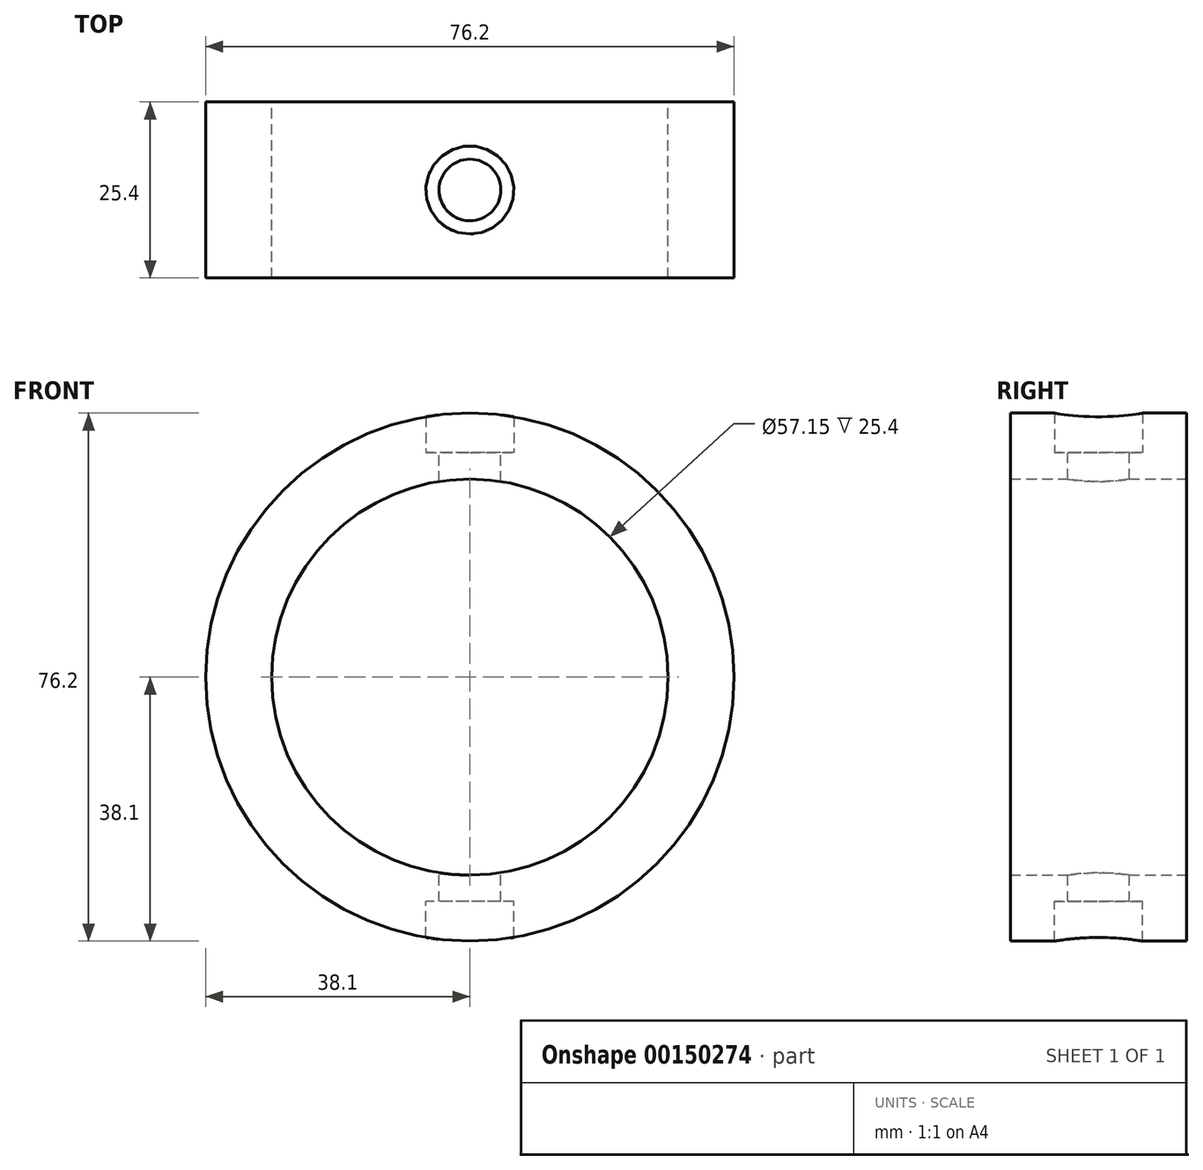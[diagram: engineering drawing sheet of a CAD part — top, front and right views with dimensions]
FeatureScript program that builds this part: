
annotation { "Feature Type Name" : "Feature", "Feature Type Description" : "" }
export const myFeature = defineFeature(function(context is Context, id is Id, definition is map)
    precondition{}
    {
        {
            var Q0;
            Q0=qCreatedBy(makeId("Front.planeOp"),FACE);
            var sketch = newSketch(context, id + "F0", { "sketchPlane" : qUnion([Q0])});
            skCircle(sketch, "E0", {"center": v(0, 0) * mm, "radius": 38.1 * mm});
            skCircle(sketch, "E1", {"center": v(0, 0) * mm, "radius": 28.58 * mm});
            skSolve(sketch);
        }
        {
            var Q0;
            Q0=makeQuery(id+"F0.imprint","IMPRINT",FACE,{"disambiguationData":[TD([[makeQuery(id+"F0.imprint","IMPRINT",EDGE,{"derivedFrom":sQuery(id+"F0.wireOp",EDGE,"E0")}),1.0]])]});
            extrude(context, id + "F1", {"entities" : qUnion([Q0]), "depth" : 25.4 * mm});
        }
        {
            var Q0;
            Q0=qCreatedBy(makeId("Top.planeOp"),FACE);
            var sketch = newSketch(context, id + "F2", { "sketchPlane" : qUnion([Q0])});
            skCircle(sketch, "E2", {"center": v(0, -12.7) * mm, "radius": 4.44 * mm});
            skLineSegment(sketch, "E3", {"start": v(38.1, 0) * mm, "end": v(38.1, -25.4) * mm});
            skLineSegment(sketch, "E4", {"start": v(-38.1, -25.4) * mm, "end": v(-38.1, 0) * mm});
            skSolve(sketch);
        }
        {
            var Q0;
            Q0=makeQuery(id+"F2.imprint","IMPRINT",FACE,{"disambiguationData":[TD([[makeQuery(id+"F2.imprint","IMPRINT",EDGE,{"derivedFrom":sQuery(id+"F2.wireOp",EDGE,"E2")}),1.0]])]});
            extrude(context, id + "F3", {"entities" : qUnion([Q0]), "operationType" : NewBodyOperationType.REMOVE, "endBound" : BoundingType.SYMMETRIC, "oppositeDirection" : true, "depth" : 76.2 * mm});
        }
        {
            var Q0;
            Q0=qCreatedBy(makeId("Top.planeOp"),FACE);
            cPlane(context, id + "F4", {"entities" : qUnion([Q0]), "cplaneType" : CPlaneType.OFFSET, "offset" : 32.38 * mm, "width" : 152.4 * mm, "height" : 152.4 * mm});
        }
        {
            var Q0;
            Q0=qCreatedBy(id+"F4.planeOp",FACE);
            var sketch = newSketch(context, id + "F5", { "sketchPlane" : qUnion([Q0])});
            skCircle(sketch, "E5", {"center": v(0, -12.7) * mm, "radius": 6.35 * mm});
            skLineSegment(sketch, "E6", {"start": v(38.1, 0) * mm, "end": v(38.1, -25.4) * mm});
            skLineSegment(sketch, "E7", {"start": v(-38.1, -25.4) * mm, "end": v(-38.1, 0) * mm});
            skCircle(sketch, "E8.0", {"center": v(0, -12.7) * mm, "radius": 4.44 * mm});
            skSolve(sketch);
        }
        {
            var Q0;
            Q0 = qSketchRegion(id + "F5", true);
            extrude(context, id + "F6", {"entities" : qUnion([Q0]), "operationType" : NewBodyOperationType.REMOVE, "depth" : 25.4 * mm});
        }
        {
            var Q0;
            Q0=qCreatedBy(makeId("Top.planeOp"),FACE);
            cPlane(context, id + "F7", {"entities" : qUnion([Q0]), "cplaneType" : CPlaneType.OFFSET, "offset" : 32.38 * mm, "oppositeDirection" : true, "width" : 152.4 * mm, "height" : 152.4 * mm});
        }
        {
            var Q0;
            Q0=qCreatedBy(id+"F7.planeOp",FACE);
            var sketch = newSketch(context, id + "F8", { "sketchPlane" : qUnion([Q0])});
            skCircle(sketch, "E9", {"center": v(0, -12.7) * mm, "radius": 6.35 * mm});
            skCircle(sketch, "E10.0", {"center": v(0, -12.7) * mm, "radius": 4.44 * mm});
            skSolve(sketch);
        }
        {
            var Q0;
            Q0 = qSketchRegion(id + "F8", true);
            extrude(context, id + "F9", {"entities" : qUnion([Q0]), "operationType" : NewBodyOperationType.REMOVE, "oppositeDirection" : true, "depth" : 25.4 * mm});
        }
    });
